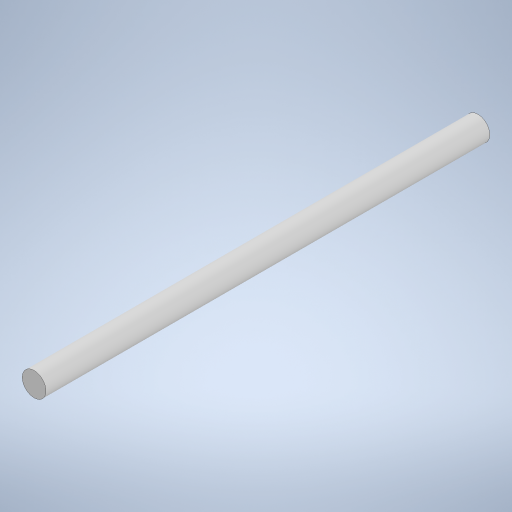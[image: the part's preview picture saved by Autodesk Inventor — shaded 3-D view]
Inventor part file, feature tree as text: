
AUTODESK INVENTOR PART (.ipt)
format: ipt  version: 2023 (Build 270158000, 158)  size: 229,888 bytes
history: native  units: mm
features: extrude x1, sketch x1
ambient origin geometry x8: Origin, YZ Plane, XZ Plane, XY Plane, X Axis, Y Axis, Z Axis, Center Point
bodies: Solid1 (feature_tree)
feature tree (2):
  extrude  "Extrusion1"  Depth=150.0mm TaperAngle=0.0deg
  sketch  "Sketch1"  dims[d0=8.0mm d1=150.0mm d2=0.0mm]
